FCSTD DOCUMENT  (FreeCAD 0.19R0.19.2)
Label: headphoneStand
License: All rights reserved
LicenseURL: http://en.wikipedia.org/wiki/All_rights_reserved
objects: Sketcher::SketchObject×1
note: 1 computed .brp shape members not serialized (recipe doc carries the construction recipe); baked Part::Feature solids carry a one-line shape summary decoded from their .brp

FEATURE [Sketcher::SketchObject] Sketch
  FullyConstrained = false
  sketch-geometry (91):
    g0: LineSegment StartX=0 StartY=0 StartZ=0 EndX=-1.5309 EndY=0 EndZ=0
    g1: LineSegment StartX=0 StartY=5.04081 StartZ=0 EndX=-1.51927 EndY=5.04081 EndZ=0
    g2: LineSegment StartX=-1.51927 StartY=5.04081 StartZ=0 EndX=-1.51927 EndY=10.1697 EndZ=0
    g3: LineSegment StartX=-1.5309 StartY=0 StartZ=0 EndX=-1.5309 EndY=-5.21292 EndZ=0
    g4: LineSegment StartX=-1.51927 StartY=10.1697 StartZ=0 EndX=-4.04717 EndY=10.1697 EndZ=0
    g5: LineSegment StartX=-1.5309 StartY=-5.21292 StartZ=0 EndX=-3.98642 EndY=-5.21292 EndZ=0
    g6: Circle CenterX=-4.04717 CenterY=10.1695 CenterZ=0 NormalX=0 NormalY=0 NormalZ=1 AngleXU=0 Radius=1
    g7: Circle CenterX=-9.99602 CenterY=2.47228 CenterZ=0 NormalX=0 NormalY=0 NormalZ=1 AngleXU=0 Radius=1
    g8: Circle CenterX=-3.98642 CenterY=-5.21292 CenterZ=0 NormalX=0 NormalY=0 NormalZ=1 AngleXU=0 Radius=1
    g9: BSplineCurve PolesCount=3 KnotsCount=2 Degree=2 IsPeriodic=0
    g10: GeomPoint X=-4.04717 Y=10.1695 Z=0
    g11: GeomPoint X=-3.98642 Y=-5.21292 Z=0
    g12: LineSegment StartX=0 StartY=34.0653 StartZ=0 EndX=0 EndY=5.04081 EndZ=0
    g13: LineSegment StartX=-1.51927 StartY=39.1061 StartZ=0 EndX=-1.51927 EndY=44.2348 EndZ=0
    g14: LineSegment StartX=-1.5309 StartY=34.0653 StartZ=0 EndX=-1.5309 EndY=28.8523 EndZ=0
    g15: LineSegment StartX=-1.51927 StartY=44.2348 StartZ=0 EndX=-4.04717 EndY=44.2348 EndZ=0
    g16: LineSegment StartX=-1.5309 StartY=28.8523 StartZ=0 EndX=-3.98642 EndY=28.8523 EndZ=0
    g17: Circle CenterX=-4.04717 CenterY=44.2348 CenterZ=0 NormalX=0 NormalY=0 NormalZ=1 AngleXU=0 Radius=1
    g18: Circle CenterX=-3.98642 CenterY=28.8523 CenterZ=0 NormalX=0 NormalY=0 NormalZ=1 AngleXU=0 Radius=1
    g19: BSplineCurve PolesCount=3 KnotsCount=2 Degree=2 IsPeriodic=0
    g20: GeomPoint X=-4.04717 Y=44.2348 Z=0
    g21: GeomPoint X=-3.98642 Y=28.8523 Z=0
    g22: LineSegment StartX=0 StartY=39.1061 StartZ=0 EndX=-1.51927 EndY=39.1061 EndZ=0
    g23: LineSegment StartX=0 StartY=34.0653 StartZ=0 EndX=-1.5309 EndY=34.0653 EndZ=0
    g24: LineSegment StartX=-1.51927 StartY=73.1267 StartZ=0 EndX=-1.51927 EndY=78.2554 EndZ=0
    g25: LineSegment StartX=-1.5309 StartY=68.0859 StartZ=0 EndX=-1.5309 EndY=62.8729 EndZ=0
    g26: LineSegment StartX=-1.51927 StartY=78.2554 StartZ=0 EndX=-4.04717 EndY=78.2554 EndZ=0
    g27: LineSegment StartX=-1.5309 StartY=62.8729 StartZ=0 EndX=-3.98642 EndY=62.8729 EndZ=0
    g28: Circle CenterX=-4.04717 CenterY=78.2554 CenterZ=0 NormalX=0 NormalY=0 NormalZ=1 AngleXU=0 Radius=1
    g29: Circle CenterX=-3.98642 CenterY=62.8729 CenterZ=0 NormalX=0 NormalY=0 NormalZ=1 AngleXU=0 Radius=1
    g30: BSplineCurve PolesCount=3 KnotsCount=2 Degree=2 IsPeriodic=0
    g31: GeomPoint X=-4.04717 Y=78.2554 Z=0
    g32: GeomPoint X=-3.98642 Y=62.8729 Z=0
    g33: LineSegment StartX=0 StartY=73.1267 StartZ=0 EndX=-1.51927 EndY=73.1267 EndZ=0
    g34: LineSegment StartX=0 StartY=68.0859 StartZ=0 EndX=-1.5309 EndY=68.0859 EndZ=0
    g35: LineSegment StartX=0 StartY=68.0859 StartZ=0 EndX=0 EndY=39.1061 EndZ=0
    g36: LineSegment StartX=55.9714 StartY=45.0131 StartZ=0 EndX=47.9365 EndY=45.0131 EndZ=0
    g37: LineSegment StartX=55.9714 StartY=20.0333 StartZ=0 EndX=55.9714 EndY=45.0131 EndZ=0
    g38: LineSegment StartX=0 StartY=73.1267 StartZ=0 EndX=0 EndY=78.2549 EndZ=0
    g39: LineSegment StartX=0 StartY=78.2549 StartZ=0 EndX=1.02877 EndY=78.2549 EndZ=0
    g40: Circle CenterX=1.02877 CenterY=78.2549 CenterZ=0 NormalX=0 NormalY=0 NormalZ=1 AngleXU=0 Radius=1
    g41: Circle CenterX=7.98777 CenterY=61.6212 CenterZ=0 NormalX=0 NormalY=0 NormalZ=1 AngleXU=0 Radius=1
    g42: Circle CenterX=7.98777 CenterY=45.0131 CenterZ=0 NormalX=0 NormalY=0 NormalZ=1 AngleXU=0 Radius=1
    g43: BSplineCurve PolesCount=3 KnotsCount=2 Degree=2 IsPeriodic=0
    g44: GeomPoint X=1.02877 Y=78.2549 Z=0
    g45: GeomPoint X=7.98777 Y=45.0131 Z=0
    g46: Circle CenterX=7.98777 CenterY=36.0353 CenterZ=0 NormalX=0 NormalY=0 NormalZ=1 AngleXU=0 Radius=1
    g47: Circle CenterX=7.98777 CenterY=32.5409 CenterZ=0 NormalX=0 NormalY=0 NormalZ=1 AngleXU=0 Radius=1
    g48: Circle CenterX=11.4386 CenterY=31.9944 CenterZ=0 NormalX=0 NormalY=0 NormalZ=1 AngleXU=0 Radius=1
    g49: BSplineCurve PolesCount=3 KnotsCount=2 Degree=2 IsPeriodic=0
    g50: GeomPoint X=7.98777 Y=36.0353 Z=0
    g51: GeomPoint X=11.4386 Y=31.9944 Z=0
    g52: LineSegment StartX=7.98777 StartY=45.0131 StartZ=0 EndX=7.98777 EndY=36.0353 EndZ=0
    g53: Circle CenterX=47.9365 CenterY=36.0282 CenterZ=0 NormalX=0 NormalY=0 NormalZ=1 AngleXU=0 Radius=1
    g54: Circle CenterX=47.9365 CenterY=32.4999 CenterZ=0 NormalX=0 NormalY=0 NormalZ=1 AngleXU=0 Radius=1
    g55: Circle CenterX=44.5192 CenterY=31.9623 CenterZ=0 NormalX=0 NormalY=0 NormalZ=1 AngleXU=0 Radius=1
    g56: BSplineCurve PolesCount=3 KnotsCount=2 Degree=2 IsPeriodic=0
    g57: GeomPoint X=47.9365 Y=36.0282 Z=0
    g58: GeomPoint X=44.5192 Y=31.9623 Z=0
    g59: LineSegment StartX=47.9365 StartY=45.0131 StartZ=0 EndX=47.9365 EndY=36.0282 EndZ=0
    g60: Circle CenterX=11.4386 CenterY=31.9944 CenterZ=0 NormalX=0 NormalY=0 NormalZ=1 AngleXU=0 Radius=1
    g61: Circle CenterX=28.035 CenterY=29.0677 CenterZ=0 NormalX=0 NormalY=0 NormalZ=1 AngleXU=0 Radius=1
    g62: Circle CenterX=44.5192 CenterY=31.9623 CenterZ=0 NormalX=0 NormalY=0 NormalZ=1 AngleXU=0 Radius=1
    g63: BSplineCurve PolesCount=3 KnotsCount=2 Degree=2 IsPeriodic=0
    g64: GeomPoint X=11.4386 Y=31.9944 Z=0
    g65: GeomPoint X=44.5192 Y=31.9623 Z=0
    g66: LineSegment StartX=55.9714 StartY=20.0333 StartZ=0 EndX=55.9705 EndY=23.539 EndZ=0
    g67: LineSegment StartX=55.9714 StartY=20.0333 StartZ=0 EndX=52.4303 EndY=20.0333 EndZ=0
    g68: Circle CenterX=52.4303 CenterY=20.0333 CenterZ=0 NormalX=0 NormalY=0 NormalZ=1 AngleXU=0 Radius=1
    g69: Circle CenterX=55.9714 CenterY=20.0333 CenterZ=0 NormalX=0 NormalY=0 NormalZ=1 AngleXU=0 Radius=1
    g70: Circle CenterX=55.9705 CenterY=23.539 CenterZ=0 NormalX=0 NormalY=0 NormalZ=1 AngleXU=0 Radius=1
    g71: BSplineCurve PolesCount=3 KnotsCount=2 Degree=2 IsPeriodic=0
    g72: GeomPoint X=52.4303 Y=20.0333 Z=0
    g73: GeomPoint X=55.9705 Y=23.539 Z=0
    g74: LineSegment StartX=0 StartY=-20.2076 StartZ=0 EndX=0.983266 EndY=-20.2076 EndZ=0
    g75: LineSegment StartX=0 StartY=0 StartZ=0 EndX=0 EndY=-20.2076 EndZ=0
    g76: Circle CenterX=4.47075 CenterY=-13.2519 CenterZ=0 NormalX=0 NormalY=0 NormalZ=1 AngleXU=0 Radius=1
    g77: Circle CenterX=9.98794 CenterY=10.1697 CenterZ=0 NormalX=0 NormalY=0 NormalZ=1 AngleXU=0 Radius=1
    g78: Circle CenterX=52.4303 CenterY=20.0333 CenterZ=0 NormalX=0 NormalY=0 NormalZ=1 AngleXU=0 Radius=1
    g79: BSplineCurve PolesCount=3 KnotsCount=2 Degree=2 IsPeriodic=0
    g80: GeomPoint X=4.47075 Y=-13.2519 Z=0
    g81: GeomPoint X=52.4303 Y=20.0333 Z=0
    g82-g86: Circle x5 (B-spline internal-alignment scaffolding for g87; pole/knot coordinates omitted)
    g87: BSplineCurve PolesCount=5 KnotsCount=3 Degree=3 IsPeriodic=0
    g88: GeomPoint X=0.983266 Y=-20.2076 Z=0
    g89: GeomPoint X=3.68451 Y=-17.8003 Z=0
    g90: GeomPoint X=4.47075 Y=-13.2519 Z=0
  constraints (132):
    c: PointOnObject(g0,g-1)
    c: PointOnObject(g1,g-2)
    c: Horizontal(g1)
    c: Coincident(g2,g1)
    c: Vertical(g2)
    c: Coincident(g3,g0)
    c: Vertical(g3)
    c: Coincident(g4,g2)
    c: Horizontal(g4)
    c: Coincident(g5,g3)
    c: Horizontal(g5)
    c: Weight(g6) = 1
    c: Equal(g6,g7)
    c: Equal(g6,g8)
    c: Coincident(g9,g5)
    c: InternalAlignment(g6,g9)
    c: InternalAlignment(g7,g9)
    c: InternalAlignment(g8,g9)
    c: Coincident(g12,g1)
    c: Vertical(g12)
    c: Horizontal(g22)
    c: Coincident(g13,g22)
    c: Vertical(g13)
    c: Coincident(g14,g23)
    c: Vertical(g14)
    c: Coincident(g15,g13)
    c: Horizontal(g15)
    c: Coincident(g16,g14)
    c: Horizontal(g16)
    c: Weight(g17) = 1
    c: Equal(g17,g18)
    c: Coincident(g19,g16)
    c: InternalAlignment(g17,g19)
    c: InternalAlignment(g18,g19)
    c: Coincident(g23,g12)
    c: PointOnObject(g34,g-2)
    c: Horizontal(g33)
    c: Coincident(g24,g33)
    c: Vertical(g24)
    c: Coincident(g25,g34)
    c: Vertical(g25)
    c: Coincident(g26,g24)
    c: Horizontal(g26)
    c: Coincident(g27,g25)
    c: Horizontal(g27)
    c: Weight(g28) = 1
    c: Equal(g28,g29)
    c: Coincident(g30,g27)
    c: InternalAlignment(g28,g30)
    c: InternalAlignment(g29,g30)
    c: Coincident(g35,g34)
    c: Vertical(g37)
    c: Coincident(g36,g37)
    c: Horizontal(g36)
    c: Coincident(g38,g33)
    c: PointOnObject(g38,g-2)
    c: Vertical(g38)
    c: Coincident(g39,g38)
    c: Horizontal(g39)
    c: Coincident(g43,g39)
    c: Weight(g40) = 1
    c: Equal(g40,g41)
    c: Equal(g40,g42)
    c: InternalAlignment(g40,g43)
    c: InternalAlignment(g41,g43)
    c: InternalAlignment(g42,g43)
    c: InternalAlignment(g44,g43)
    c: InternalAlignment(g45,g43)
    c: Weight(g46) = 1
    c: Equal(g46,g47)
    c: Equal(g46,g48)
    c: InternalAlignment(g46,g49)
    c: InternalAlignment(g47,g49)
    c: InternalAlignment(g48,g49)
    c: InternalAlignment(g50,g49)
    c: InternalAlignment(g51,g49)
    c: Coincident(g52,g43)
    c: Coincident(g52,g49)
    c: Vertical(g52)
    c: Weight(g53) = 1
    c: Equal(g53,g54)
    c: Equal(g53,g55)
    c: InternalAlignment(g53,g56)
    c: InternalAlignment(g54,g56)
    c: InternalAlignment(g55,g56)
    c: InternalAlignment(g57,g56)
    c: InternalAlignment(g58,g56)
    c: Coincident(g59,g36)
    c: Coincident(g59,g56)
    c: Vertical(g59)
    c: Weight(g60) = 1
    c: Equal(g60,g61)
    c: Equal(g60,g62)
    c: InternalAlignment(g60,g63)
    c: InternalAlignment(g61,g63)
    c: InternalAlignment(g62,g63)
    c: InternalAlignment(g64,g63)
    c: InternalAlignment(g65,g63)
    c: Coincident(g66,g37)
    c: Coincident(g67,g37)
    c: Horizontal(g67)
    c: Coincident(g71,g67)
    c: Weight(g68) = 1
    c: Equal(g68,g69)
    c: Coincident(g69,g37)
    c: Equal(g68,g70)
    c: Coincident(g71,g66)
    c: InternalAlignment(g68,g71)
    c: InternalAlignment(g69,g71)
    c: InternalAlignment(g70,g71)
    c: InternalAlignment(g72,g71)
    c: InternalAlignment(g73,g71)
    c: Horizontal(g74)
    c: Coincident(g75,g0)
    c: Coincident(g75,g74)
    c: Vertical(g75)
    c: Weight(g76) = 1
    c: Equal(g76,g77)
    c: Equal(g76,g78)
    c: Coincident(g79,g67)
    c: InternalAlignment(g76,g79)
    c: InternalAlignment(g77,g79)
    c: InternalAlignment(g78,g79)
    c: InternalAlignment(g80,g79)
    c: InternalAlignment(g81,g79)
    c: Coincident(g87,g74)
    c: Weight(g82) = 1
    c: Equal(g82, g83-g86) x4
    c: InternalAlignment(g82-g86 -> g87) x5
    c: InternalAlignment(g88,g87)
    c: InternalAlignment(g89,g87)
    c: InternalAlignment(g90,g87)
